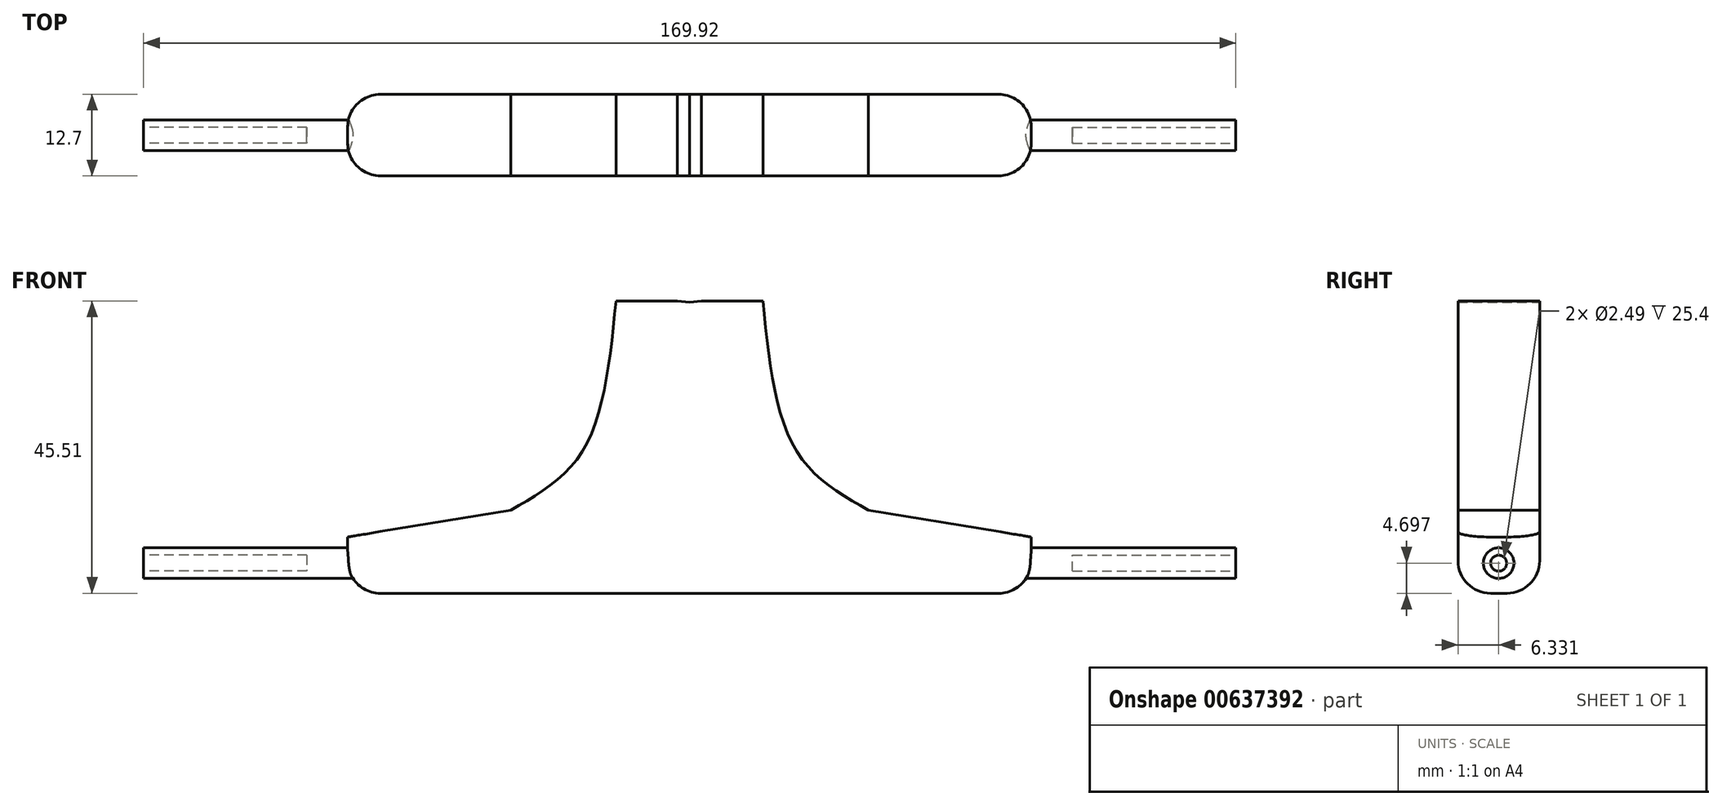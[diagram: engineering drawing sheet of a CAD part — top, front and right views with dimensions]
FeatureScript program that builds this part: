
annotation { "Feature Type Name" : "Feature", "Feature Type Description" : "" }
export const myFeature = defineFeature(function(context is Context, id is Id, definition is map)
    precondition{}
    {
        {
            var Q0;
            Q0=qCreatedBy(makeId("Front.planeOp"),FACE);
            var sketch = newSketch(context, id + "F0", { "sketchPlane" : qUnion([Q0])});
            skLineSegment(sketch, "E0", {"start": v(0, 7.5) * mm, "end": v(-53.17, 7.5) * mm});
            skLineSegment(sketch, "E1", {"start": v(-53.17, 7.5) * mm, "end": v(-53.17, 16.27) * mm});
            skLineSegment(sketch, "E2", {"start": v(-53.17, 16.27) * mm, "end": v(-27.8, 20.47) * mm});
            skLineSegment(sketch, "E3", {"start": v(-11.43, 53) * mm, "end": v(-1.87, 53) * mm});
            skLineSegment(sketch, "E4", {"start": v(-1.87, 53) * mm, "end": v(0, 52.86) * mm});
            skFitSpline(sketch, "E5", {"points": [v(-27.8, 20.47) * mm, v(-16.64, 29.66) * mm, v(-11.43, 53) * mm], "startDerivative": vector(29.07, 16.53) * mm, "endDerivative": vector(4.68, 47.26) * mm});
            skLineSegment(sketch, "E6.MirrorCS", {"start": v(1.87, 53) * mm, "end": v(0, 52.86) * mm});
            skLineSegment(sketch, "E7.MirrorCS", {"start": v(11.43, 53) * mm, "end": v(1.87, 53) * mm});
            skFitSpline(sketch, "E8.MirrorCS", {"points": [v(27.8, 20.47) * mm, v(16.64, 29.66) * mm, v(11.43, 53) * mm], "startDerivative": vector(-29.07, 16.53) * mm, "endDerivative": vector(-4.68, 47.26) * mm});
            skLineSegment(sketch, "E9.MirrorCS", {"start": v(53.17, 16.27) * mm, "end": v(27.8, 20.47) * mm});
            skLineSegment(sketch, "E10.MirrorCS", {"start": v(53.17, 7.5) * mm, "end": v(53.17, 16.27) * mm});
            skLineSegment(sketch, "E11.MirrorCS", {"start": v(0, 7.5) * mm, "end": v(53.17, 7.5) * mm});
            skSolve(sketch);
        }
        {
            var Q0;
            Q0=qSketchRegion(id+"F0",true);
            extrude(context, id + "F1", {"entities" : qUnion([Q0]), "depth" : 12.7 * mm, "offsetDistance" : 25.4 * mm});
        }
        {
            var Q0;
            Q0=makeQuery(id+"F1.opExtrude","SWEPT_FACE",FACE,{"disambiguationData":[OSD([sQuery(id+"F0.wireOp",EDGE,"E1")])]});
            var sketch = newSketch(context, id + "F2", { "sketchPlane" : qUnion([Q0])});
            skCircle(sketch, "E12", {"center": v(6.37, 12.2) * mm, "radius": 2.38 * mm});
            skSolve(sketch);
        }
        {
            var Q0;
            Q0=makeQuery(id+"F2.imprint","IMPRINT",FACE,{"disambiguationData":[TD([[makeQuery(id+"F2.imprint","IMPRINT",EDGE,{"derivedFrom":sQuery(id+"F2.wireOp",EDGE,"E12")}),1.0]])]});
            extrude(context, id + "F3", {"entities" : qUnion([Q0]), "operationType" : NewBodyOperationType.ADD, "depth" : 31.75 * mm, "offsetDistance" : 25.4 * mm, "hasSecondDirection" : true, "secondDirectionOppositeDirection" : true, "secondDirectionDepth" : 138.18 * mm});
        }
        {
            var Q0;
            Q0=makeQuery(id+"F1.opExtrude","CAP_EDGE",EDGE,{"disambiguationData":[OSD([sQuery(id+"F0.wireOp",EDGE,"E0"),sQuery(id+"F0.wireOp",EDGE,"E11.MirrorCS")])],"isStart":true});
            fillet(context, id + "F4", {"entities" : qUnion([Q0]), "radius" : 5.08 * mm, "tangentPropagation" : true, "allowEdgeOverflow" : false});
        }
        {
            var Q0;
            Q0=makeQuery(id+"F4.opFillet","BLEND_EDGE",EDGE,{"blendedFrom":[makeQuery(id+"F1.opExtrude","CAP_EDGE",EDGE,{"disambiguationData":[OSD([sQuery(id+"F0.wireOp",EDGE,"E0"),sQuery(id+"F0.wireOp",EDGE,"E11.MirrorCS")])],"isStart":true}),makeQuery(id+"F1.opExtrude","SWEPT_FACE",FACE,{"disambiguationData":[OSD([sQuery(id+"F0.wireOp",EDGE,"E1")])]})],"blendedInto":[makeQuery(id+"F1.opExtrude","SWEPT_FACE",FACE,{"disambiguationData":[OSD([sQuery(id+"F0.wireOp",EDGE,"E1")])]})]});
            fillet(context, id + "F5", {"entities" : qUnion([Q0]), "radius" : 5.08 * mm, "tangentPropagation" : true, "allowEdgeOverflow" : false});
        }
        {
            var Q0;
            {var subQ0=sQuery(id+"F0.wireOp",EDGE,"E1");var subQ1=sQuery(id+"F0.wireOp",EDGE,"E0");Q0=makeQuery(id+"F5.opFillet","BLEND_EDGE",EDGE,{"blendedFrom":[makeQuery(id+"F1.opExtrude","SWEPT_EDGE",EDGE,{"disambiguationData":[OSD([subQ1,subQ0])]}),makeQuery(id+"F1.opExtrude","CAP_FACE",FACE,{"disambiguationData":[OSD([subQ1,subQ0,sQuery(id+"F0.wireOp",EDGE,"E2"),sQuery(id+"F0.wireOp",EDGE,"E3"),sQuery(id+"F0.wireOp",EDGE,"E4"),sQuery(id+"F0.wireOp",EDGE,"E5"),sQuery(id+"F0.wireOp",EDGE,"E6.MirrorCS"),sQuery(id+"F0.wireOp",EDGE,"E7.MirrorCS"),sQuery(id+"F0.wireOp",EDGE,"E8.MirrorCS"),sQuery(id+"F0.wireOp",EDGE,"E9.MirrorCS"),sQuery(id+"F0.wireOp",EDGE,"E10.MirrorCS"),sQuery(id+"F0.wireOp",EDGE,"E11.MirrorCS")])],"isStart":false})],"blendedInto":[makeQuery(id+"F1.opExtrude","CAP_FACE",FACE,{"disambiguationData":[OSD([subQ1,subQ0,sQuery(id+"F0.wireOp",EDGE,"E2"),sQuery(id+"F0.wireOp",EDGE,"E3"),sQuery(id+"F0.wireOp",EDGE,"E4"),sQuery(id+"F0.wireOp",EDGE,"E5"),sQuery(id+"F0.wireOp",EDGE,"E6.MirrorCS"),sQuery(id+"F0.wireOp",EDGE,"E7.MirrorCS"),sQuery(id+"F0.wireOp",EDGE,"E8.MirrorCS"),sQuery(id+"F0.wireOp",EDGE,"E9.MirrorCS"),sQuery(id+"F0.wireOp",EDGE,"E10.MirrorCS"),sQuery(id+"F0.wireOp",EDGE,"E11.MirrorCS")])],"isStart":false})]});}
            fillet(context, id + "F6", {"entities" : qUnion([Q0]), "radius" : 5.08 * mm, "tangentPropagation" : true, "allowEdgeOverflow" : false});
        }
        {
            var Q0;
            Q0=makeQuery(id+"F3.opExtrude","CAP_FACE",FACE,{"disambiguationData":[OSD([sQuery(id+"F2.wireOp",EDGE,"E12")])],"isStart":false});
            var sketch = newSketch(context, id + "F7", { "sketchPlane" : qUnion([Q0])});
            skCircle(sketch, "E13", {"center": v(6.37, 12.2) * mm, "radius": 1.25 * mm});
            skSolve(sketch);
        }
        {
            var Q0;
            Q0=makeQuery(id+"F7.imprint","IMPRINT",FACE,{"disambiguationData":[TD([[makeQuery(id+"F7.imprint","IMPRINT",EDGE,{"derivedFrom":sQuery(id+"F7.wireOp",EDGE,"E13")}),1.0]])]});
            extrude(context, id + "F8", {"entities" : qUnion([Q0]), "operationType" : NewBodyOperationType.REMOVE, "oppositeDirection" : true, "depth" : 25.4 * mm, "offsetDistance" : 25.4 * mm});
        }
        {
            var Q0;
            Q0=makeQuery(id+"F1.opExtrude","CAP_EDGE",EDGE,{"disambiguationData":[OSD([sQuery(id+"F0.wireOp",EDGE,"E10.MirrorCS")])],"isStart":false});
            fillet(context, id + "F9", {"entities" : qUnion([Q0]), "radius" : 5.08 * mm, "tangentPropagation" : true, "allowEdgeOverflow" : false});
        }
        {
            var Q0;
            Q0=makeQuery(id+"F3.opExtrude","CAP_FACE",FACE,{"disambiguationData":[OSD([sQuery(id+"F2.wireOp",EDGE,"E12")])],"isStart":true});
            var sketch = newSketch(context, id + "F10", { "sketchPlane" : qUnion([Q0])});
            skCircle(sketch, "E14", {"center": v(-6.37, 12.2) * mm, "radius": 1.25 * mm});
            skSolve(sketch);
        }
        {
            var Q0;
            Q0=makeQuery(id+"F10.imprint","IMPRINT",FACE,{"disambiguationData":[TD([[makeQuery(id+"F10.imprint","IMPRINT",EDGE,{"derivedFrom":sQuery(id+"F10.wireOp",EDGE,"E14")}),1.0]])]});
            extrude(context, id + "F11", {"entities" : qUnion([Q0]), "operationType" : NewBodyOperationType.REMOVE, "oppositeDirection" : true, "depth" : 25.4 * mm, "offsetDistance" : 25.4 * mm});
        }
    });
